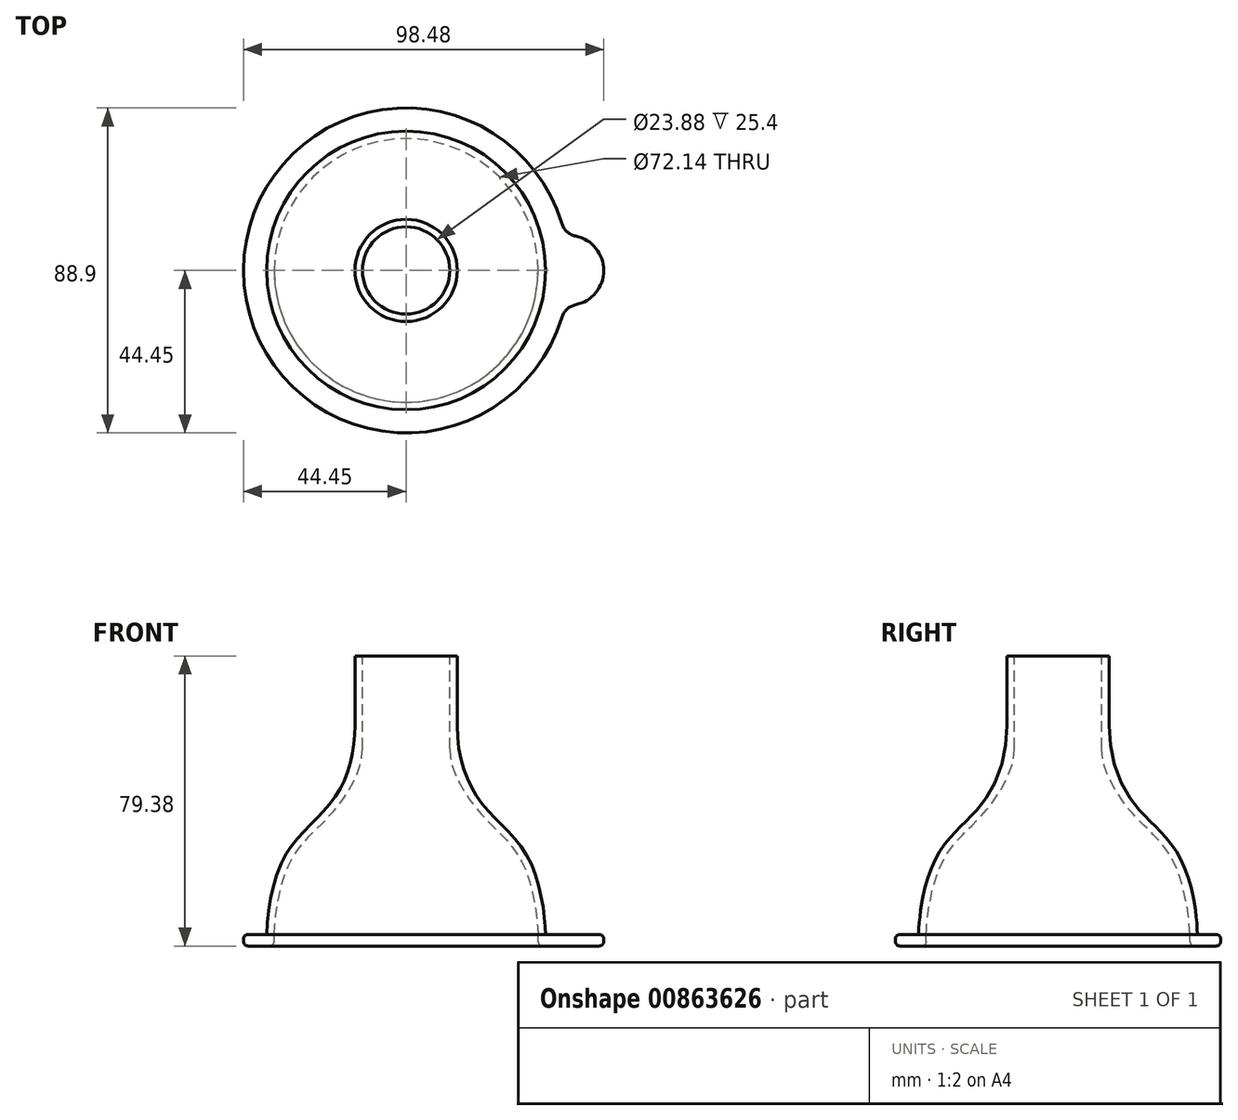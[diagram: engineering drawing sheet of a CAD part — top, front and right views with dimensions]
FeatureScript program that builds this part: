
annotation { "Feature Type Name" : "Feature", "Feature Type Description" : "" }
export const myFeature = defineFeature(function(context is Context, id is Id, definition is map)
    precondition{}
    {
        {
            var Q0;
            Q0=qCreatedBy(makeId("Front.planeOp"),FACE);
            var sketch = newSketch(context, id + "F0", { "sketchPlane" : qUnion([Q0])});
            skLineSegment(sketch, "E0", {"start": v(11.94, 50.8) * mm, "end": v(11.94, 76.2) * mm});
            skLineSegment(sketch, "E1", {"start": v(11.94, 76.2) * mm, "end": v(13.97, 76.2) * mm});
            skLineSegment(sketch, "E2", {"start": v(13.97, 76.2) * mm, "end": v(13.97, 57.15) * mm});
            skLineSegment(sketch, "E3", {"start": v(36.07, 0) * mm, "end": v(38.1, 0) * mm});
            skFitSpline(sketch, "E4", {"points": [v(11.94, 50.8) * mm, v(20.1, 33.43) * mm, v(31.93, 19.3) * mm, v(36.07, 0) * mm], "startDerivative": vector(0, -53.16) * mm, "endDerivative": vector(1.8, -38.02) * mm});
            skFitSpline(sketch, "E5", {"points": [v(13.97, 57.15) * mm, v(20.52, 36.07) * mm, v(33.3, 21.08) * mm, v(38.1, 0) * mm], "startDerivative": vector(0, -75.57) * mm, "endDerivative": vector(0.9, -45.18) * mm});
            skLineSegment(sketch, "E6", {"start": v(0, 76.2) * mm, "end": v(0, 0) * mm, "construction": true});
            skLineSegment(sketch, "E7", {"start": v(20.52, 36.07) * mm, "end": v(18.91, 34.83) * mm, "construction": true});
            skLineSegment(sketch, "E8", {"start": v(31.93, 19.3) * mm, "end": v(33.76, 20.19) * mm, "construction": true});
            skSolve(sketch);
        }
        {
            var Q0;
            Q0 = qSketchRegion(id + "F0", true);
            var Q1;
            Q1=sQuery(id+"F0.wireOp",EDGE,"E6");
            revolve(context, id + "F1", {"surfaceOperationType" : NewSurfaceOperationType.NEW, "entities" : qUnion([Q0]), "axis" : qUnion([Q1]), "revolveType" : RevolveType.FULL});
        }
        {
            var Q0;
            Q0=makeQuery(id+"F1.opRevolve","SWEPT_FACE",FACE,{"disambiguationData":[OSD([sQuery(id+"F0.wireOp",EDGE,"E3")])]});
            var sketch = newSketch(context, id + "F2", { "sketchPlane" : qUnion([Q0])});
            skCircle(sketch, "E9", {"center": v(0, 0) * mm, "radius": 36.07 * mm});
            skPoint(sketch, "E10", {"position": v(38.1, 0) * mm});
            skPoint(sketch, "E11", {"position": v(44.45, 0) * mm});
            skArc(sketch, "E12", {"start": v(43.42, -9.53) * mm, "mid": v(54.03, 0) * mm, "end": v(43.42, 9.52) * mm});
            skArc(sketch, "E13", {"start": v(43.42, 9.53) * mm, "mid": v(-44.45, 0) * mm, "end": v(43.42, -9.53) * mm});
            skArc(sketch, "E14", {"start": v(43.42, -9.52) * mm, "mid": v(44.45, 0) * mm, "end": v(43.42, 9.52) * mm, "construction": true});
            skSolve(sketch);
        }
        {
            var Q0;
            Q0 = qSketchRegion(id + "F2", true);
            extrude(context, id + "F3", {"entities" : qUnion([Q0]), "operationType" : NewBodyOperationType.ADD, "depth" : 3.17 * mm, "offsetDistance" : 25.4 * mm});
        }
        {
            var Q0;
            Q0=makeQuery(id+"F1.opRevolve","SWEPT_EDGE",EDGE,{"disambiguationData":[OSD([sQuery(id+"F0.wireOp",EDGE,"E3"),sQuery(id+"F0.wireOp",EDGE,"E5")])]});
            var Q1;
            {var subQ0=sQuery(id+"F2.wireOp",EDGE,"E13");var subQ1=sQuery(id+"F2.wireOp",EDGE,"E12");Q1=makeQuery(id+"F3.opExtrude","SWEPT_EDGE",EDGE,{"disambiguationData":[OSD([subQ1,subQ0]),TDD([makeQuery(id+"F2.imprint","INTERSECT",VERTEX,{"disambiguationData":[OD(1.0)],"derivedFrom":[subQ1,subQ0]})])]});}
            var Q2;
            {var subQ0=sQuery(id+"F2.wireOp",EDGE,"E13");var subQ1=sQuery(id+"F2.wireOp",EDGE,"E12");Q2=makeQuery(id+"F3.opExtrude","SWEPT_EDGE",EDGE,{"disambiguationData":[OSD([subQ1,subQ0]),TDD([makeQuery(id+"F2.imprint","INTERSECT",VERTEX,{"disambiguationData":[OD(0.0)],"derivedFrom":[subQ1,subQ0]})])]});}
            fillet(context, id + "F4", {"entities" : qUnion([Q0, Q1, Q2]), "radius" : 5.08 * mm, "tangentPropagation" : true, "allowEdgeOverflow" : false});
        }
        {
            var Q0;
            Q0=makeQuery(id+"F3.opExtrude","CAP_EDGE",EDGE,{"disambiguationData":[OSD([sQuery(id+"F2.wireOp",EDGE,"E9")])],"isStart":false});
            var Q1;
            Q1=makeQuery(id+"F3.opExtrude","CAP_EDGE",EDGE,{"disambiguationData":[OSD([sQuery(id+"F2.wireOp",EDGE,"E13")])],"isStart":true});
            var Q2;
            Q2=makeQuery(id+"F3.opExtrude","CAP_EDGE",EDGE,{"disambiguationData":[OSD([sQuery(id+"F2.wireOp",EDGE,"E13")])],"isStart":false});
            fillet(context, id + "F5", {"entities" : qUnion([Q0, Q1, Q2]), "radius" : 1.27 * mm, "tangentPropagation" : true, "allowEdgeOverflow" : false});
        }
    });
